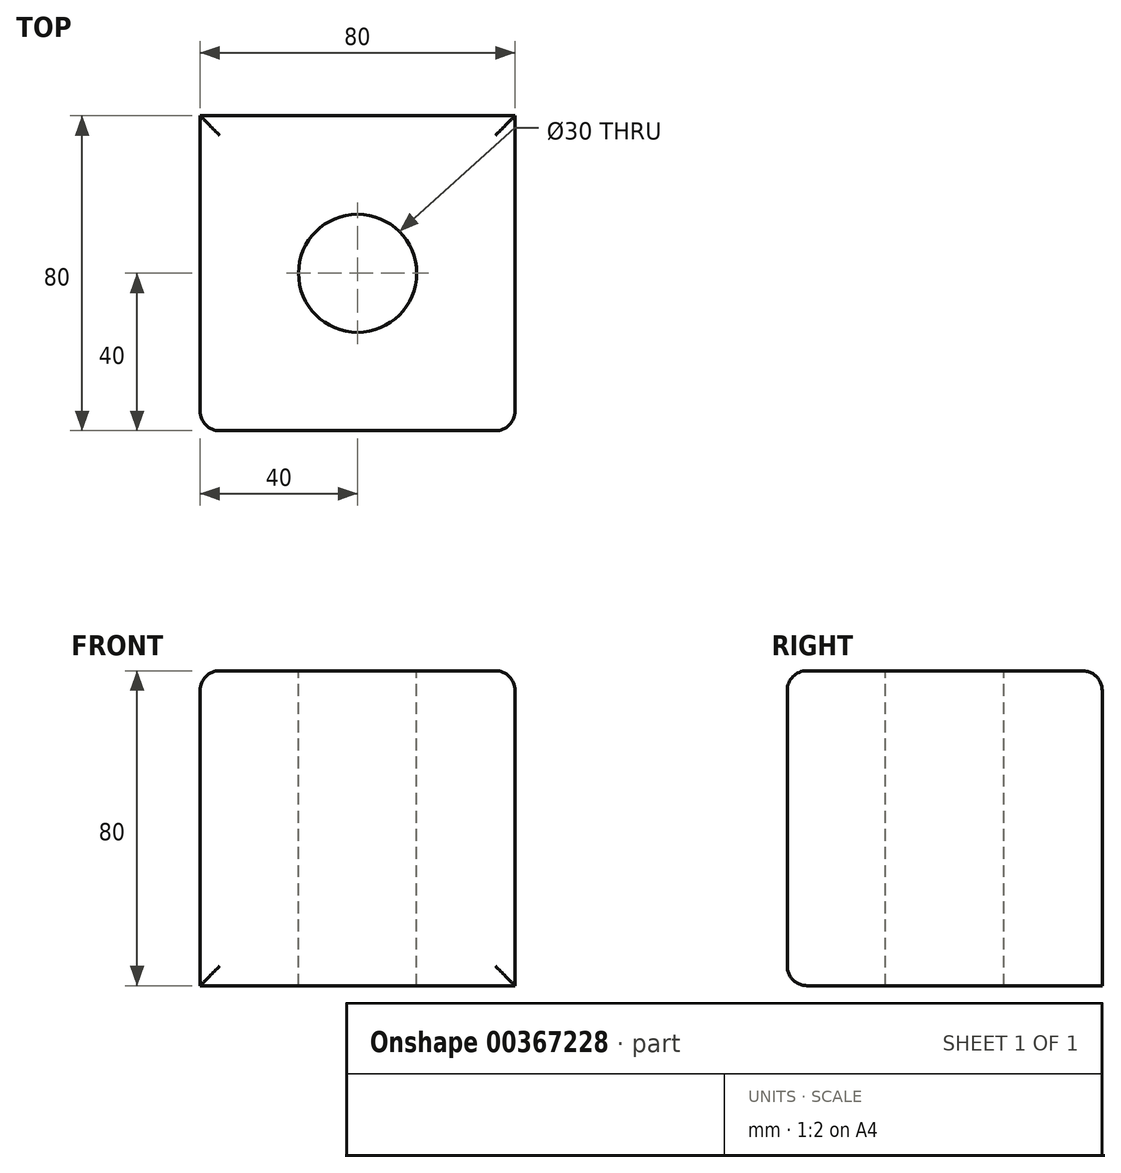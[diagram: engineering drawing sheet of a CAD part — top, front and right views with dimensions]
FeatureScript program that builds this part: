
annotation { "Feature Type Name" : "Feature", "Feature Type Description" : "" }
export const myFeature = defineFeature(function(context is Context, id is Id, definition is map)
    precondition{}
    {
        {
            var Q0;
            Q0=qCreatedBy(makeId("Top.planeOp"),FACE);
            var sketch = newSketch(context, id + "F0", { "sketchPlane" : qUnion([Q0])});
            skLineSegment(sketch, "E0.bottom", {"start": v(-40, 40) * mm, "end": v(40, 40) * mm});
            skLineSegment(sketch, "E0.top", {"start": v(-40, -40) * mm, "end": v(40, -40) * mm});
            skLineSegment(sketch, "E0.left", {"start": v(-40, 40) * mm, "end": v(-40, -40) * mm});
            skLineSegment(sketch, "E0.right", {"start": v(40, 40) * mm, "end": v(40, -40) * mm});
            skPoint(sketch, "E0.middle", {"position": v(0, 0) * mm});
            skSolve(sketch);
        }
        {
            var Q0;
            Q0 = qSketchRegion(id + "F0", true);
            var Q1;
            Q1=makeQuery(id+"F0.imprint","IMPRINT",FACE,{"disambiguationData":[TD([[makeQuery(id+"F0.imprint","IMPRINT",EDGE,{"derivedFrom":sQuery(id+"F0.wireOp",EDGE,"E0.bottom")}),-1.0]])]});
            extrude(context, id + "F1", {"entities" : qUnion([Q0, Q1]), "depth" : 80 * mm});
        }
        {
            var Q0;
            Q0=makeQuery(id+"F1.opExtrude","CAP_FACE",FACE,{"disambiguationData":[OSD([sQuery(id+"F0.wireOp",EDGE,"E0.bottom"),sQuery(id+"F0.wireOp",EDGE,"E0.top"),sQuery(id+"F0.wireOp",EDGE,"E0.left"),sQuery(id+"F0.wireOp",EDGE,"E0.right")])],"isStart":false});
            var sketch = newSketch(context, id + "F2", { "sketchPlane" : qUnion([Q0])});
            skCircle(sketch, "E1", {"center": v(0, 0) * mm, "radius": 15 * mm});
            skSolve(sketch);
        }
        {
            var Q0;
            Q0=makeQuery(id+"F2.imprint","IMPRINT",FACE,{"disambiguationData":[TD([[makeQuery(id+"F2.imprint","IMPRINT",EDGE,{"derivedFrom":sQuery(id+"F2.wireOp",EDGE,"E1")}),1.0]])]});
            extrude(context, id + "F3", {"entities" : qUnion([Q0]), "operationType" : NewBodyOperationType.REMOVE, "endBound" : BoundingType.THROUGH_ALL, "oppositeDirection" : true, "depth" : 25 * mm});
        }
        {
            var Q0;
            Q0=makeQuery(id+"F1.opExtrude","CAP_EDGE",EDGE,{"disambiguationData":[OSD([sQuery(id+"F0.wireOp",EDGE,"E0.bottom")])],"isStart":false});
            var Q1;
            Q1=makeQuery(id+"F1.opExtrude","CAP_EDGE",EDGE,{"disambiguationData":[OSD([sQuery(id+"F0.wireOp",EDGE,"E0.left")])],"isStart":false});
            var Q2;
            Q2=makeQuery(id+"F1.opExtrude","CAP_EDGE",EDGE,{"disambiguationData":[OSD([sQuery(id+"F0.wireOp",EDGE,"E0.right")])],"isStart":false});
            var Q3;
            Q3=makeQuery(id+"F1.opExtrude","CAP_EDGE",EDGE,{"disambiguationData":[OSD([sQuery(id+"F0.wireOp",EDGE,"E0.top")])],"isStart":false});
            var Q4;
            Q4=makeQuery(id+"F1.opExtrude","SWEPT_EDGE",EDGE,{"disambiguationData":[OSD([sQuery(id+"F0.wireOp",EDGE,"E0.top"),sQuery(id+"F0.wireOp",EDGE,"E0.left")])]});
            var Q5;
            Q5=makeQuery(id+"F1.opExtrude","CAP_EDGE",EDGE,{"disambiguationData":[OSD([sQuery(id+"F0.wireOp",EDGE,"E0.top")])],"isStart":true});
            var Q6;
            Q6=makeQuery(id+"F1.opExtrude","SWEPT_FACE",FACE,{"disambiguationData":[OSD([sQuery(id+"F0.wireOp",EDGE,"E0.top")])]});
            var Q7;
            Q7=makeQuery(id+"F1.opExtrude","SWEPT_EDGE",EDGE,{"disambiguationData":[OSD([sQuery(id+"F0.wireOp",EDGE,"E0.top"),sQuery(id+"F0.wireOp",EDGE,"E0.right")])]});
            fillet(context, id + "F4", {"entities" : qUnion([Q0, Q1, Q2, Q3, Q4, Q5, Q6, Q7]), "radius" : 5 * mm, "tangentPropagation" : true, "allowEdgeOverflow" : false});
        }
    });
